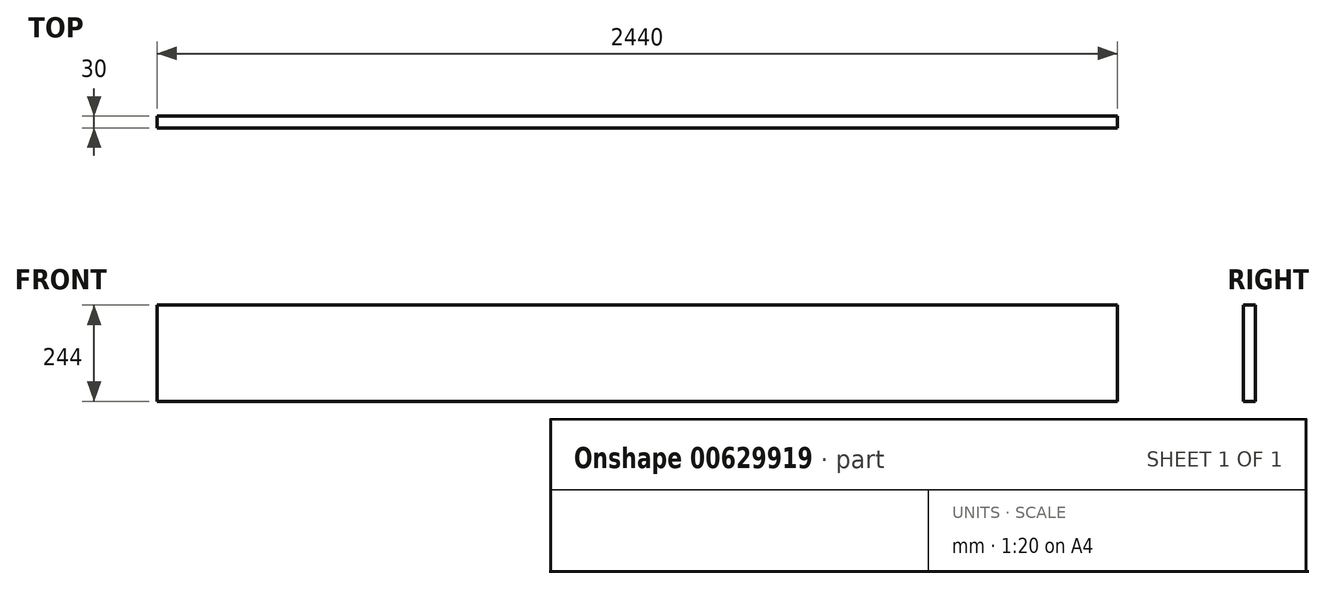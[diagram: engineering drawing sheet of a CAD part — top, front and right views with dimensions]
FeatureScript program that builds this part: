
annotation { "Feature Type Name" : "Feature", "Feature Type Description" : "" }
export const myFeature = defineFeature(function(context is Context, id is Id, definition is map)
    precondition{}
    {
        {
            var Q0;
            Q0=qCreatedBy(makeId("Front.planeOp"),FACE);
            var sketch = newSketch(context, id + "F0", { "sketchPlane" : qUnion([Q0])});
            skLineSegment(sketch, "E0.bottom", {"start": v(0, 0) * mm, "end": v(2440, 0) * mm});
            skLineSegment(sketch, "E0.top", {"start": v(0, 244) * mm, "end": v(2440, 244) * mm});
            skLineSegment(sketch, "E0.left", {"start": v(0, 0) * mm, "end": v(0, 244) * mm});
            skLineSegment(sketch, "E0.right", {"start": v(2440, 0) * mm, "end": v(2440, 244) * mm});
            skSolve(sketch);
        }
        {
            var Q0;
            Q0=makeQuery(id+"F0.imprint","IMPRINT",FACE,{"disambiguationData":[TD([[makeQuery(id+"F0.imprint","IMPRINT",EDGE,{"derivedFrom":sQuery(id+"F0.wireOp",EDGE,"E0.bottom")}),1.0]])]});
            extrude(context, id + "F1", {"entities" : qUnion([Q0]), "depth" : 30 * mm, "offsetDistance" : 25 * mm});
        }
    });
